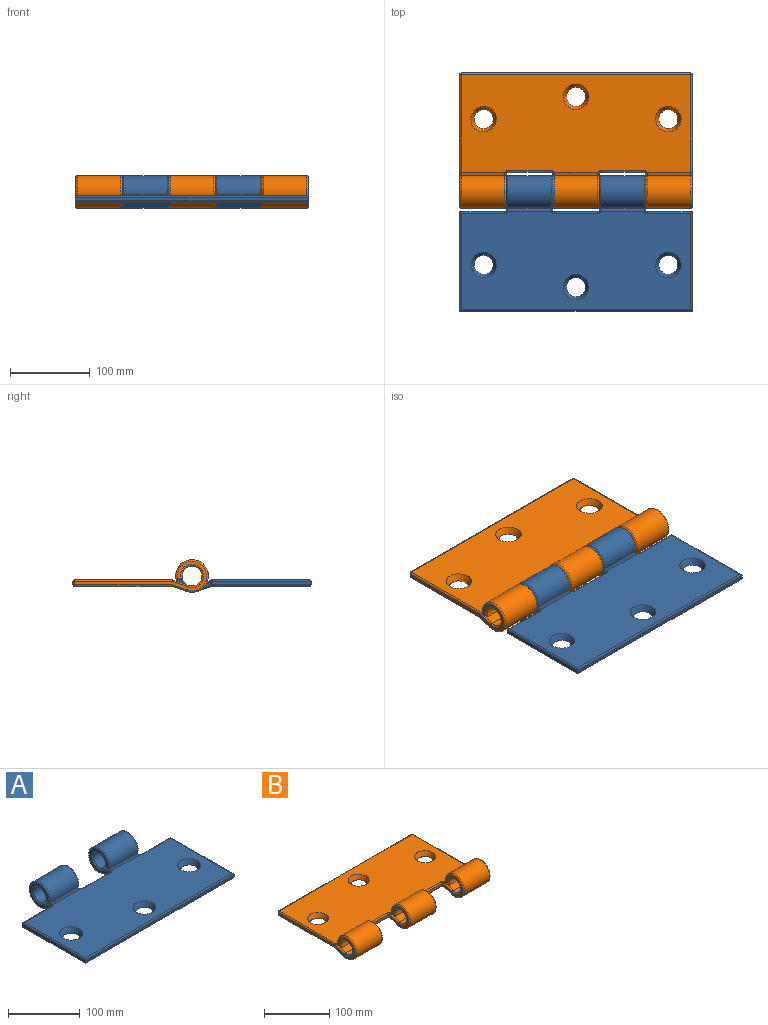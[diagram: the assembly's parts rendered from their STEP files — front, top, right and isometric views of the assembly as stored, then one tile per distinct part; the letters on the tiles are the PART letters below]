
ASSEMBLY  parts=2 mates=1
PART A: 83 faces, bbox 292x171.7x44.4 mm
  f0: plane 54.86x18.04mm, normal (0,-0.33,-0.94), area 1040.3mm2, adj f2,f14,f59,f63,f81,f82
  f1: plane 54.86x18.04mm, normal (0,-0.33,-0.94), area 1040.3mm2, adj f3,f14,f38,f43,f54,f58
  f2: cylinder r=20.5mm len=54.4mm, axis (-1,0,0), area 5813.8mm2, adj f0,f67,f74,f79
  f3: cylinder r=20.5mm len=54.4mm, axis (-1,0,0), area 5813.8mm2, adj f1,f33,f42,f50
  f4: plane 54.4x6.8mm, normal (0,0,-1), area 369.8mm2, adj f6,f68,f74,f75
  f5: plane 54.4x6.8mm, normal (0,0,-1), area 369.8mm2, adj f7,f32,f41,f42
  f6: cylinder r=12.5mm len=54.4mm, axis (-1,0,0), area 3700mm2, adj f4,f8,f64,f72
  f7: cylinder r=12.5mm len=54.4mm, axis (-1,0,0), area 3700mm2, adj f5,f9,f29,f36
  f8: plane 56.19x20.94mm, normal (0,0.31,0.95), area 1200.4mm2, adj f6,f12,f52,f56,f60,f61,f65,f69
  f9: plane 56.19x20.94mm, normal (0,0.31,0.95), area 1200.4mm2, adj f7,f12,f30,f31,f34,f35,f39,f44
  f10: plane 124.66x4mm, normal (1,0,0), area 498.7mm2, adj f13,f19,f45,f70
  f11: plane 124.66x4mm, normal (-1,0,0), area 498.7mm2, adj f13,f24,f53,f76
  f12: plane 288x122.66mm, normal (0,0,1), area 32568.4mm2, adj f8,f9,f15,f16,f17,f35,f40,f44
  f13: plane 292x4mm, normal (0,-1,0), area 1168mm2, adj f10,f11,f49,f73
  f14: plane 288x122.72mm, normal (0,0,-1), area 33624mm2, adj f0,f1,f15,f16,f17,f43,f47,f51
  f15: cone r=12mm half-angle=26.6deg, axis (0,0,1), area 786.8mm2, adj f12,f14
  f16: cone r=12mm half-angle=26.6deg, axis (0,0,1), area 786.8mm2, adj f12,f14
  f17: cone r=12mm half-angle=26.6deg, axis (0,0,1), area 786.8mm2, adj f12,f14
  f18: plane 41.34x37mm, normal (1,0,0), area 415.2mm2, adj f25,f31,f36,f41,f50,f54
  f19: plane 56.4x4mm, normal (0,1,0), area 225.6mm2, adj f10,f25,f40,f66
  f20: plane 41.34x37mm, normal (1,0,0), area 415.2mm2, adj f26,f60,f63,f64,f67,f68
  f21: plane 54.4x4mm, normal (0,1,0), area 217.6mm2, adj f26,f27,f48,f51
  f22: plane 41.34x37mm, normal (-1,0,0), area 415.2mm2, adj f27,f29,f32,f33,f34,f38
  f23: plane 41.34x37mm, normal (-1,0,0), area 415.2mm2, adj f28,f69,f72,f75,f79,f81
  f24: plane 56.4x4mm, normal (0,1,0), area 225.6mm2, adj f11,f28,f57,f78
  f25: cylinder r=2mm len=4.58mm, axis (0,0,-1), area 12.3mm2, adj f18,f19,f30,f35,f58,f62
  f26: cylinder r=2mm len=4.58mm, axis (0,0,-1), area 12.3mm2, adj f20,f21,f52,f55,f56,f59
  f27: cylinder r=2mm len=4.58mm, axis (0,0,1), area 12.3mm2, adj f21,f22,f39,f43,f44,f47
  f28: cylinder r=2mm len=4.58mm, axis (0,0,1), area 12.3mm2, adj f23,f24,f61,f65,f80,f82
  f29: torus R=14.5mm, axis (1,0,0), area 221.8mm2, adj f7,f22,f32,f34
  f30: bspline ~2.73x2.53mm, area 5.9mm2, adj f9,f25,f31,f35
  f31: cylinder r=2mm len=18.94mm, axis (0,0.95,-0.31), area 60.6mm2, adj f9,f18,f30,f36
  f32: cylinder r=2mm len=6.8mm, axis (0,1,0), area 17.1mm2, adj f5,f22,f29,f37
  f33: torus R=18.5mm, axis (1,0,0), area 323.8mm2, adj f3,f22,f37,f38
  f34: cylinder r=2mm len=18.94mm, axis (0,-0.95,0.31), area 60.6mm2, adj f9,f22,f29,f39
  f35: torus R=4mm, axis (0,0,1), area 8.7mm2, adj f9,f12,f25,f30,f40
  f36: torus R=14.5mm, axis (1,0,0), area 221.8mm2, adj f7,f18,f31,f41
  f37: sphere r=2mm, area 8.1mm2, adj f32,f33,f42
  f38: cylinder r=2mm len=17.36mm, axis (0,0.94,-0.33), area 55.6mm2, adj f1,f22,f33,f43
  f39: bspline ~2.73x2.53mm, area 5.9mm2, adj f9,f27,f34,f44
  f40: cylinder r=2mm len=56.4mm, axis (-1,0,0), area 174mm2, adj f12,f19,f35,f45
  f41: cylinder r=2mm len=6.8mm, axis (0,-1,0), area 17.1mm2, adj f5,f18,f36,f46
  f42: cylinder r=2mm len=54.4mm, axis (-1,0,0), area 153.2mm2, adj f3,f5,f37,f46
  f43: bspline ~2.47x2.32mm, area 3.5mm2, adj f1,f14,f27,f38,f47
  f44: torus R=4mm, axis (0,0,1), area 8.7mm2, adj f9,f12,f27,f39,f48
  f45: cylinder r=2mm len=124.66mm, axis (0,1,0), area 385.4mm2, adj f10,f12,f40,f49
  f46: sphere r=2mm, area 5.8mm2, adj f41,f42,f50
  f47: torus R=4mm, axis (0,0,1), area 9.2mm2, adj f14,f27,f43,f51
  f48: cylinder r=2mm len=54.4mm, axis (-1,0,0), area 170.9mm2, adj f12,f21,f44,f52
  f49: cylinder r=2mm len=292mm, axis (1,0,0), area 911.1mm2, adj f12,f13,f45,f53
  f50: torus R=18.5mm, axis (1,0,0), area 323.8mm2, adj f3,f18,f46,f54
  f51: cylinder r=2mm len=54.4mm, axis (1,0,0), area 170.9mm2, adj f14,f21,f47,f55
  f52: torus R=4mm, axis (0,0,1), area 8.7mm2, adj f8,f12,f26,f48,f56
  f53: cylinder r=2mm len=124.66mm, axis (0,-1,0), area 385.4mm2, adj f11,f12,f49,f57
  f54: cylinder r=2mm len=17.36mm, axis (0,-0.94,0.33), area 55.6mm2, adj f1,f18,f50,f58
  f55: torus R=4mm, axis (0,0,1), area 9.2mm2, adj f14,f26,f51,f59
  f56: bspline ~2.73x2.53mm, area 5.9mm2, adj f8,f26,f52,f60
  f57: cylinder r=2mm len=56.4mm, axis (-1,0,0), area 174mm2, adj f12,f24,f53,f61
  f58: bspline ~3.16x2.89mm, area 3.5mm2, adj f1,f14,f25,f54,f62
  f59: bspline ~3.16x2.89mm, area 3.5mm2, adj f0,f14,f26,f55,f63
  f60: cylinder r=2mm len=18.94mm, axis (0,0.95,-0.31), area 60.6mm2, adj f8,f20,f56,f64
  f61: torus R=4mm, axis (0,0,1), area 8.7mm2, adj f8,f12,f28,f57,f65
  f62: torus R=4mm, axis (0,0,1), area 9.2mm2, adj f14,f25,f58,f66
  f63: cylinder r=2mm len=17.36mm, axis (0,-0.94,0.33), area 55.6mm2, adj f0,f20,f59,f67
  f64: torus R=14.5mm, axis (1,0,0), area 221.8mm2, adj f6,f20,f60,f68
  f65: bspline ~3.65x3.1mm, area 5.9mm2, adj f8,f28,f61,f69
  f66: cylinder r=2mm len=56.4mm, axis (1,0,0), area 174mm2, adj f14,f19,f62,f70
  f67: torus R=18.5mm, axis (1,0,0), area 323.8mm2, adj f2,f20,f63,f71
  f68: cylinder r=2mm len=6.8mm, axis (0,-1,0), area 17.1mm2, adj f4,f20,f64,f71
  f69: cylinder r=2mm len=18.94mm, axis (0,-0.95,0.31), area 60.6mm2, adj f8,f23,f65,f72
  f70: cylinder r=2mm len=124.66mm, axis (0,-1,0), area 385.4mm2, adj f10,f14,f66,f73
  f71: sphere r=2mm, area 5.6mm2, adj f67,f68,f74
  f72: torus R=14.5mm, axis (1,0,0), area 221.8mm2, adj f6,f23,f69,f75
  f73: cylinder r=2mm len=292mm, axis (-1,0,0), area 911.1mm2, adj f13,f14,f70,f76
  f74: cylinder r=2mm len=54.4mm, axis (-1,0,0), area 153.2mm2, adj f2,f4,f71,f77
  f75: cylinder r=2mm len=6.8mm, axis (0,1,0), area 17.1mm2, adj f4,f23,f72,f77
  f76: cylinder r=2mm len=124.66mm, axis (0,1,0), area 385.4mm2, adj f11,f14,f73,f78
  f77: sphere r=2mm, area 8.1mm2, adj f74,f75,f79
  f78: cylinder r=2mm len=56.4mm, axis (1,0,0), area 174mm2, adj f14,f24,f76,f80
  f79: torus R=18.5mm, axis (1,0,0), area 323.8mm2, adj f2,f23,f77,f81
  f80: torus R=4mm, axis (0,0,1), area 9.2mm2, adj f14,f28,f78,f82
  f81: cylinder r=2mm len=17.36mm, axis (0,0.94,-0.33), area 55.6mm2, adj f0,f23,f79,f82
  f82: bspline ~2.47x2.32mm, area 3.5mm2, adj f0,f14,f28,f80,f81
PART B: 98 faces, bbox 292x171.7x44.4 mm
  f0: plane 54.86x18.04mm, normal (0,0.33,-0.94), area 1040.3mm2, adj f2,f12,f42,f44,f96,f97
  f1: plane 54.63x18.04mm, normal (0,0.33,-0.94), area 1040.2mm2, adj f3,f12,f72,f87,f89
  f2: cylinder r=20.5mm len=54.4mm, axis (-1,0,0), area 5907mm2, adj f0,f4,f40,f94
  f3: cylinder r=20.5mm len=54.4mm, axis (-1,0,0), area 5813.8mm2, adj f1,f75,f81,f85
  f4: plane 54.4x8.42mm, normal (0,0,-1), area 458.3mm2, adj f2,f6,f38,f92
  f5: plane 54.4x6.8mm, normal (0,0,-1), area 369.8mm2, adj f7,f74,f80,f81
  f6: cylinder r=12.5mm len=54.4mm, axis (-1,0,0), area 3700mm2, adj f4,f8,f36,f90
  f7: cylinder r=12.5mm len=54.4mm, axis (-1,0,0), area 3700mm2, adj f5,f9,f71,f77
  f8: plane 56.19x20.94mm, normal (0,-0.31,0.95), area 1200.4mm2, adj f6,f10,f33,f34,f35,f84,f86,f88
  f9: plane 55.3x20.94mm, normal (0,-0.31,0.95), area 1199.6mm2, adj f7,f10,f69,f73,f76,f79
  f10: plane 288x122.66mm, normal (0,0,1), area 32677.2mm2, adj f8,f9,f17,f20,f21,f22,f35,f37
  f11: plane 288x4mm, normal (0,1,0), area 1152mm2, adj f60,f62,f65,f66
  f12: plane 288x122.72mm, normal (0,0,-1), area 33732.8mm2, adj f0,f1,f13,f20,f21,f22,f44,f46
  f13: plane 54.63x18.04mm, normal (0,0.33,-0.94), area 1040.2mm2, adj f12,f14,f51,f52,f58
  f14: cylinder r=20.5mm len=54.4mm, axis (-1,0,0), area 5907mm2, adj f13,f15,f49,f56
  f15: plane 54.4x8.42mm, normal (0,0,-1), area 458.3mm2, adj f14,f16,f47,f54
  f16: cylinder r=12.5mm len=54.4mm, axis (-1,0,0), area 3700mm2, adj f15,f17,f45,f53
  f17: plane 55.3x20.94mm, normal (0,-0.31,0.95), area 1199.6mm2, adj f10,f16,f39,f41,f43,f55
  f18: plane 166x37mm, normal (1,0,0), area 913.5mm2, adj f65,f67,f69,f70,f71,f72,f74,f75
  f19: plane 166x37mm, normal (-1,0,0), area 913.5mm2, adj f53,f54,f55,f56,f57,f58,f60,f61
  f20: cone r=12mm half-angle=26.6deg, axis (0,0,1), area 786.8mm2, adj f10,f12
  f21: cone r=12mm half-angle=26.6deg, axis (0,0,1), area 786.8mm2, adj f10,f12
  f22: cone r=12mm half-angle=26.6deg, axis (0,0,1), area 786.8mm2, adj f10,f12
  f23: plane 41.34x37mm, normal (-1,0,0), area 415.2mm2, adj f29,f73,f77,f80,f85,f87
  f24: plane 54.4x4mm, normal (0,-1,0), area 217.6mm2, adj f29,f30,f82,f93
  f25: plane 41.34x37mm, normal (1,0,0), area 415.2mm2, adj f30,f88,f90,f92,f94,f96
  f26: plane 41.34x37mm, normal (-1,0,0), area 415.2mm2, adj f31,f34,f36,f38,f40,f42
  f27: plane 54.4x4mm, normal (0,-1,0), area 217.6mm2, adj f31,f32,f37,f48
  f28: plane 41.34x37mm, normal (1,0,0), area 415.2mm2, adj f32,f43,f45,f47,f49,f51
  f29: cylinder r=2mm len=4.58mm, axis (0,0,1), area 12.3mm2, adj f23,f24,f76,f79,f89,f91
  f30: cylinder r=2mm len=4.58mm, axis (0,0,-1), area 12.3mm2, adj f24,f25,f84,f86,f95,f97
  f31: cylinder r=2mm len=4.58mm, axis (0,0,1), area 12.3mm2, adj f26,f27,f33,f35,f44,f46
  f32: cylinder r=2mm len=4.58mm, axis (0,0,-1), area 12.3mm2, adj f27,f28,f39,f41,f50,f52
  f33: bspline ~3.65x3.1mm, area 5.9mm2, adj f8,f31,f34,f35
  f34: cylinder r=2mm len=18.94mm, axis (0,-0.95,-0.31), area 60.6mm2, adj f8,f26,f33,f36
  f35: torus R=4mm, axis (0,0,1), area 8.7mm2, adj f8,f10,f31,f33,f37
  f36: torus R=14.5mm, axis (-1,0,0), area 221.8mm2, adj f6,f26,f34,f38
  f37: cylinder r=2mm len=54.4mm, axis (1,0,0), area 170.9mm2, adj f10,f27,f35,f39
  f38: cylinder r=2mm len=8.42mm, axis (0,1,0), area 19.6mm2, adj f4,f26,f36,f40
  f39: torus R=4mm, axis (0,0,1), area 8.7mm2, adj f10,f17,f32,f37,f41
  f40: torus R=18.5mm, axis (-1,0,0), area 326.5mm2, adj f2,f26,f38,f42
  f41: bspline ~3.65x3.1mm, area 5.9mm2, adj f17,f32,f39,f43
  f42: cylinder r=2mm len=17.36mm, axis (0,0.94,0.33), area 55.6mm2, adj f0,f26,f40,f44
  f43: cylinder r=2mm len=18.94mm, axis (0,0.95,0.31), area 60.6mm2, adj f17,f28,f41,f45
  f44: bspline ~3.16x2.89mm, area 3.5mm2, adj f0,f12,f31,f42,f46
  f45: torus R=14.5mm, axis (-1,0,0), area 221.8mm2, adj f16,f28,f43,f47
  f46: torus R=4mm, axis (0,0,1), area 9.2mm2, adj f12,f31,f44,f48
  f47: cylinder r=2mm len=8.42mm, axis (0,-1,0), area 19.6mm2, adj f15,f28,f45,f49
  f48: cylinder r=2mm len=54.4mm, axis (-1,0,0), area 170.9mm2, adj f12,f27,f46,f50
  f49: torus R=18.5mm, axis (-1,0,0), area 326.5mm2, adj f14,f28,f47,f51
  f50: torus R=4mm, axis (0,0,1), area 9.2mm2, adj f12,f32,f48,f52
  f51: cylinder r=2mm len=17.36mm, axis (0,-0.94,-0.33), area 55.6mm2, adj f13,f28,f49,f52
  f52: bspline ~2.47x2.32mm, area 3.5mm2, adj f12,f13,f32,f50,f51
  f53: torus R=14.5mm, axis (1,0,0), area 221.8mm2, adj f16,f19,f54,f55
  f54: cylinder r=2mm len=8.42mm, axis (0,-1,0), area 19.6mm2, adj f15,f19,f53,f56
  f55: cylinder r=2mm len=21.56mm, axis (0,0.95,0.31), area 68.7mm2, adj f17,f19,f53,f57
  f56: torus R=18.5mm, axis (1,0,0), area 326.5mm2, adj f14,f19,f54,f58
  f57: cylinder r=2mm len=122.66mm, axis (0,1,0), area 384.9mm2, adj f10,f19,f55,f59
  f58: cylinder r=2mm len=19.02mm, axis (0,-0.94,-0.33), area 60.6mm2, adj f13,f19,f56,f61
  f59: sphere r=2mm, area 8.6mm2, adj f57,f60,f62
  f60: cylinder r=2mm len=4mm, axis (0,0,-1), area 12.6mm2, adj f11,f19,f59,f63
  f61: cylinder r=2mm len=123.01mm, axis (0,-1,0), area 385.9mm2, adj f12,f19,f58,f63
  f62: cylinder r=2mm len=288mm, axis (1,0,0), area 904.8mm2, adj f10,f11,f59,f64
  f63: sphere r=2mm, area 8.6mm2, adj f60,f61,f66
  f64: sphere r=2mm, area 4mm2, adj f62,f65,f67
  f65: cylinder r=2mm len=4mm, axis (0,0,1), area 12.6mm2, adj f11,f18,f64,f68
  f66: cylinder r=2mm len=288mm, axis (-1,0,0), area 904.8mm2, adj f11,f12,f63,f68
  f67: cylinder r=2mm len=122.66mm, axis (0,-1,0), area 384.9mm2, adj f10,f18,f64,f69
  f68: sphere r=2mm, area 4mm2, adj f65,f66,f70
  f69: cylinder r=2mm len=21.56mm, axis (0,-0.95,-0.31), area 68.7mm2, adj f9,f18,f67,f71
  f70: cylinder r=2mm len=123.01mm, axis (0,1,0), area 385.9mm2, adj f12,f18,f68,f72
  f71: torus R=14.5mm, axis (1,0,0), area 221.8mm2, adj f7,f18,f69,f74
  f72: cylinder r=2mm len=19.02mm, axis (0,0.94,0.33), area 60.6mm2, adj f1,f18,f70,f75
  f73: cylinder r=2mm len=18.94mm, axis (0,-0.95,-0.31), area 60.6mm2, adj f9,f23,f76,f77
  f74: cylinder r=2mm len=6.8mm, axis (0,1,0), area 17.1mm2, adj f5,f18,f71,f78
  f75: torus R=18.5mm, axis (1,0,0), area 323.8mm2, adj f3,f18,f72,f78
  f76: bspline ~2.73x2.53mm, area 5.9mm2, adj f9,f29,f73,f79
  f77: torus R=14.5mm, axis (-1,0,0), area 221.8mm2, adj f7,f23,f73,f80
  f78: sphere r=2mm, area 3.9mm2, adj f74,f75,f81
  f79: torus R=4mm, axis (0,0,1), area 8.7mm2, adj f9,f10,f29,f76,f82
  f80: cylinder r=2mm len=6.8mm, axis (0,1,0), area 17.1mm2, adj f5,f23,f77,f83
  f81: cylinder r=2mm len=54.4mm, axis (-1,0,0), area 153.2mm2, adj f3,f5,f78,f83
  f82: cylinder r=2mm len=54.4mm, axis (1,0,0), area 170.9mm2, adj f10,f24,f79,f84
  f83: sphere r=2mm, area 7.7mm2, adj f80,f81,f85
  f84: torus R=4mm, axis (0,0,1), area 8.7mm2, adj f8,f10,f30,f82,f86
  f85: torus R=18.5mm, axis (-1,0,0), area 323.8mm2, adj f3,f23,f83,f87
  f86: bspline ~2.73x2.53mm, area 5.9mm2, adj f8,f30,f84,f88
  f87: cylinder r=2mm len=17.36mm, axis (0,0.94,0.33), area 55.6mm2, adj f1,f23,f85,f89
  f88: cylinder r=2mm len=18.94mm, axis (0,0.95,0.31), area 60.6mm2, adj f8,f25,f86,f90
  f89: bspline ~3.16x2.89mm, area 3.5mm2, adj f1,f12,f29,f87,f91
  f90: torus R=14.5mm, axis (-1,0,0), area 221.8mm2, adj f6,f25,f88,f92
  f91: torus R=4mm, axis (0,0,1), area 9.2mm2, adj f12,f29,f89,f93
  f92: cylinder r=2mm len=8.42mm, axis (0,-1,0), area 19.6mm2, adj f4,f25,f90,f94
  f93: cylinder r=2mm len=54.4mm, axis (-1,0,0), area 170.9mm2, adj f12,f24,f91,f95
  f94: torus R=18.5mm, axis (-1,0,0), area 326.5mm2, adj f2,f25,f92,f96
  f95: torus R=4mm, axis (0,0,1), area 9.2mm2, adj f12,f30,f93,f97
  f96: cylinder r=2mm len=17.36mm, axis (0,-0.94,-0.33), area 55.6mm2, adj f0,f25,f94,f97
  f97: bspline ~2.47x2.32mm, area 3.5mm2, adj f0,f12,f30,f95,f96
PLACE A t=(-71.68,-306.8,-20.06)mm
PLACE B t=(-71.68,-557.12,-20.06)mm
MATE parallel B.f36 <-> A.f2  axis (1,0,0) through (-13.28,-281.96,-15.06)mm
